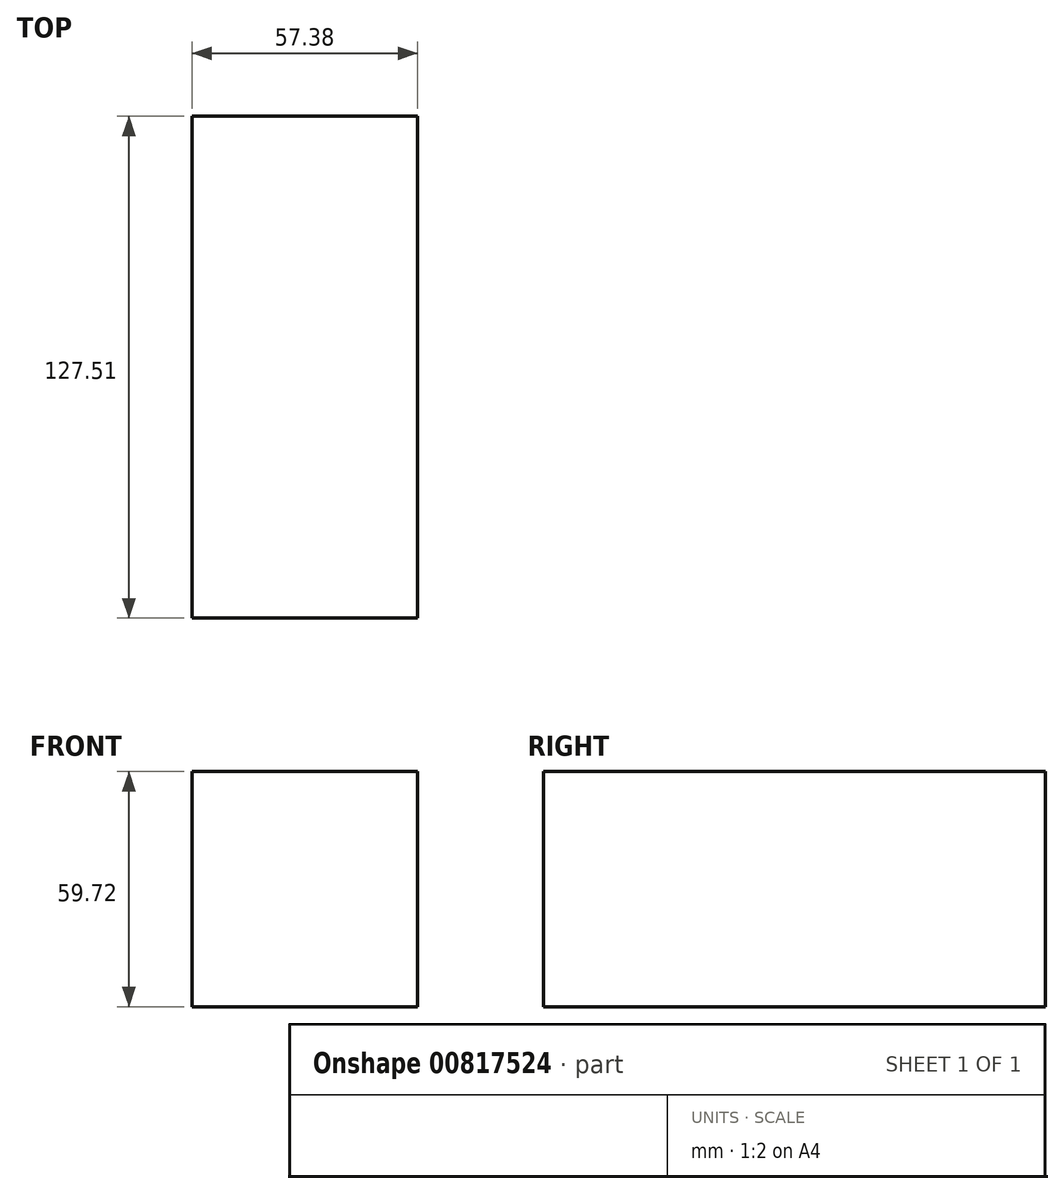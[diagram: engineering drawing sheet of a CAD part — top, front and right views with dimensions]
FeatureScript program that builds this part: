
annotation { "Feature Type Name" : "Feature", "Feature Type Description" : "" }
export const myFeature = defineFeature(function(context is Context, id is Id, definition is map)
    precondition{}
    {
        {
            var Q0;
            Q0=qCreatedBy(makeId("Front.planeOp"),FACE);
            var sketch = newSketch(context, id + "F0", { "sketchPlane" : qUnion([Q0])});
            skLineSegment(sketch, "E0.bottom", {"start": v(-128.77, 22.4) * mm, "end": v(-71.39, 22.4) * mm});
            skLineSegment(sketch, "E0.top", {"start": v(-128.77, -37.32) * mm, "end": v(-71.39, -37.32) * mm});
            skLineSegment(sketch, "E0.left", {"start": v(-128.77, 22.4) * mm, "end": v(-128.77, -37.32) * mm});
            skLineSegment(sketch, "E0.right", {"start": v(-71.39, 22.4) * mm, "end": v(-71.39, -37.32) * mm});
            skSolve(sketch);
        }
        {
            var Q0;
            Q0 = qSketchRegion(id + "F0", true);
            extrude(context, id + "F1", {"entities" : qUnion([Q0]), "oppositeDirection" : true, "depth" : 127.5 * mm, "offsetDistance" : 25.4 * mm});
        }
    });
